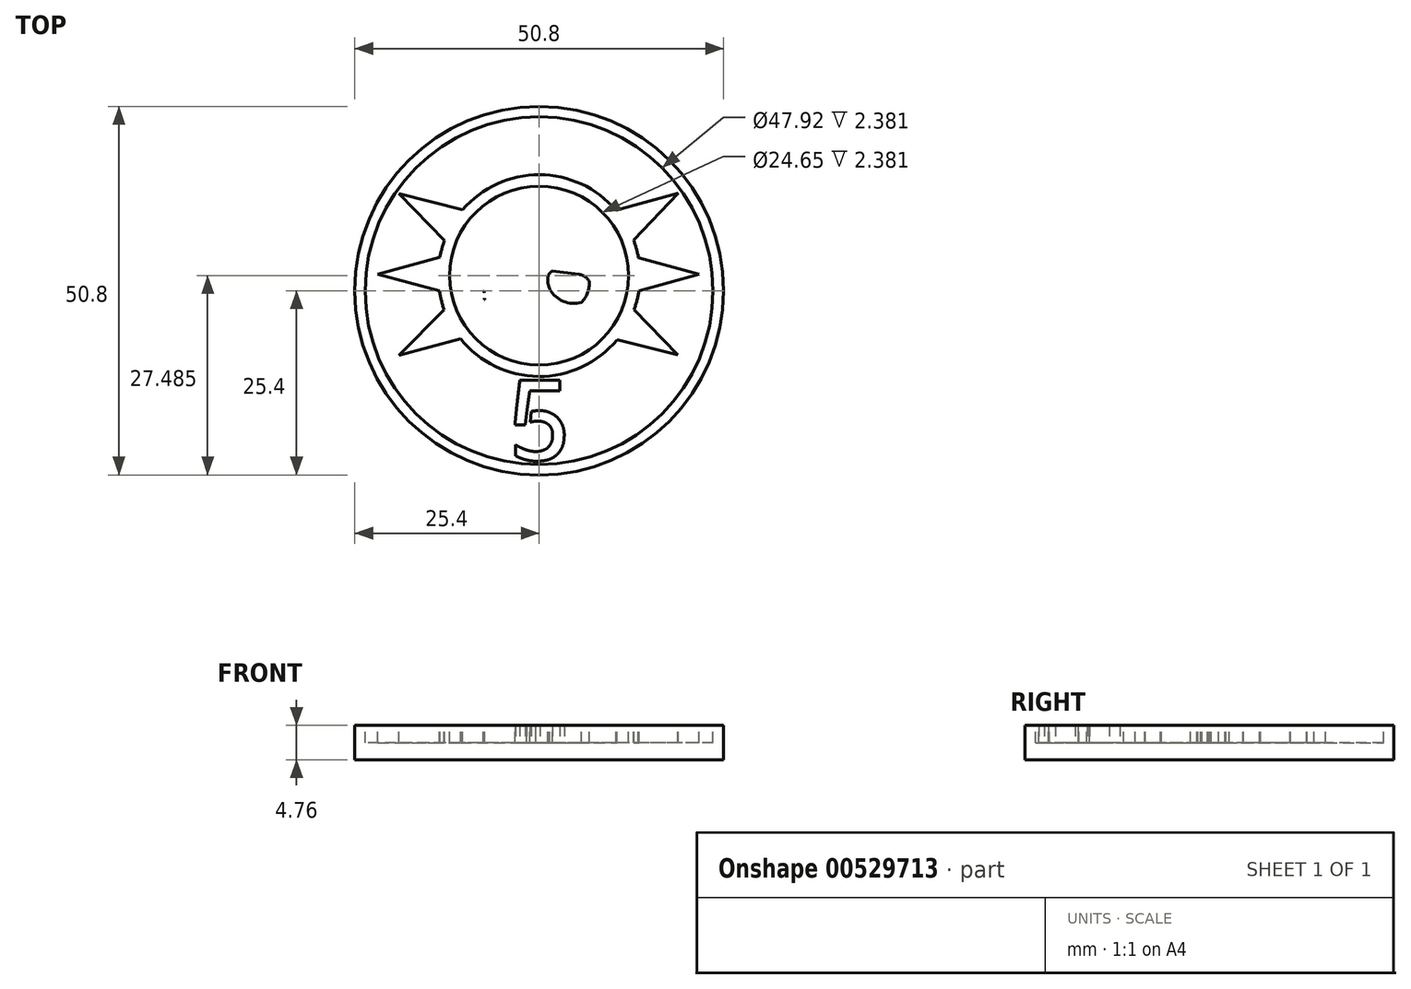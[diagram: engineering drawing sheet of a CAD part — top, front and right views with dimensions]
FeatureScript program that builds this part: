
annotation { "Feature Type Name" : "Feature", "Feature Type Description" : "" }
export const myFeature = defineFeature(function(context is Context, id is Id, definition is map)
    precondition{}
    {
        {
            var Q0;
            Q0=qCreatedBy(makeId("Top.planeOp"),FACE);
            var sketch = newSketch(context, id + "F0", { "sketchPlane" : qUnion([Q0])});
            skCircle(sketch, "E0", {"center": v(0, 0) * mm, "radius": 25.4 * mm});
            skSolve(sketch);
        }
        {
            var Q0;
            Q0=makeQuery(id+"F0.imprint","IMPRINT",FACE,{"disambiguationData":[TD([[makeQuery(id+"F0.imprint","IMPRINT",EDGE,{"derivedFrom":sQuery(id+"F0.wireOp",EDGE,"E0")}),1.0]])]});
            extrude(context, id + "F1", {"entities" : qUnion([Q0]), "depth" : 4.76 * mm, "offsetDistance" : 25.4 * mm});
        }
        {
            var Q0;
            Q0=makeQuery(id+"F1.opExtrude","CAP_FACE",FACE,{"disambiguationData":[OSD([sQuery(id+"F0.wireOp",EDGE,"E0")])],"isStart":false});
            var sketch = newSketch(context, id + "F2", { "sketchPlane" : qUnion([Q0])});
            skLineSegment(sketch, "E1", {"start": v(0, 0) * mm, "end": v(0, 25.4) * mm});
            skArc(sketch, "E2", {"start": v(-0.33, 11.95) * mm, "mid": v(-7.7, 8.08) * mm, "end": v(-7.55, -0.24) * mm});
            skLineSegment(sketch, "E3", {"start": v(-7.48, -1.06) * mm, "end": v(-7.73, -1.69) * mm});
            skArc(sketch, "E4", {"start": v(-7.55, -1.24) * mm, "mid": v(-7.44, -0.63) * mm, "end": v(-7.66, -0.06) * mm});
            skLineSegment(sketch, "E5", {"start": v(-6.9, -4.41) * mm, "end": v(-4.69, -4.62) * mm});
            skLineSegment(sketch, "E6", {"start": v(-4.56, -4.7) * mm, "end": v(-4.14, -5.5) * mm});
            skLineSegment(sketch, "E7", {"start": v(-4.12, -5.57) * mm, "end": v(-4.12, -6.26) * mm});
            skLineSegment(sketch, "E8", {"start": v(-3.62, -5.79) * mm, "end": v(-3.62, -6.3) * mm});
            skLineSegment(sketch, "E9", {"start": v(-3.22, -5.83) * mm, "end": v(-3.22, -6.7) * mm});
            skLineSegment(sketch, "E10", {"start": v(-2.5, -6.15) * mm, "end": v(-2.5, -6.76) * mm});
            skLineSegment(sketch, "E11", {"start": v(-1.96, -6.2) * mm, "end": v(-1.96, -7.04) * mm});
            skLineSegment(sketch, "E12", {"start": v(-1.28, -6.38) * mm, "end": v(-1.28, -7.15) * mm});
            skLineSegment(sketch, "E13", {"start": v(-0.76, -6.38) * mm, "end": v(-0.76, -7.25) * mm});
            skLineSegment(sketch, "E14", {"start": v(0, -6.43) * mm, "end": v(0, -7.2) * mm});
            skLineSegment(sketch, "E15", {"start": v(0.42, -6.43) * mm, "end": v(0.42, -7.2) * mm});
            skLineSegment(sketch, "E16", {"start": v(1.1, -6.35) * mm, "end": v(1.1, -7.2) * mm});
            skLineSegment(sketch, "E17", {"start": v(1.66, -6.3) * mm, "end": v(1.66, -6.98) * mm});
            skLineSegment(sketch, "E18", {"start": v(2.3, -6.14) * mm, "end": v(2.3, -6.97) * mm});
            skLineSegment(sketch, "E19", {"start": v(2.65, -6.1) * mm, "end": v(2.71, -6.42) * mm});
            skLineSegment(sketch, "E20", {"start": v(3.3, -5.72) * mm, "end": v(3.84, -4.99) * mm});
            skLineSegment(sketch, "E21", {"start": v(6.1, -4.92) * mm, "end": v(3.97, -4.92) * mm});
            skLineSegment(sketch, "E22", {"start": v(-5.43, 2.26) * mm, "end": v(-1.82, 2.72) * mm});
            skPoint(sketch, "E23", {"position": v(-6.9, 1.26) * mm});
            skPoint(sketch, "E24", {"position": v(-5.8, -1.59) * mm});
            skPoint(sketch, "E25", {"position": v(-1.48, 0.2) * mm});
            skPoint(sketch, "E26", {"position": v(-1.26, 2.12) * mm});
            skArc(sketch, "E27", {"start": v(-7.73, -1.69) * mm, "mid": v(-7.8, -3.16) * mm, "end": v(-6.97, -4.38) * mm});
            skPoint(sketch, "E28.visualSharp", {"position": v(-6.94, -4.4) * mm});
            skArc(sketch, "E28.filletArc", {"start": v(-6.97, -4.38) * mm, "mid": v(-6.93, -4.4) * mm, "end": v(-6.9, -4.41) * mm});
            skPoint(sketch, "E29.visualSharp", {"position": v(-4.6, -4.63) * mm});
            skArc(sketch, "E29.filletArc", {"start": v(-4.56, -4.7) * mm, "mid": v(-4.62, -4.65) * mm, "end": v(-4.69, -4.62) * mm});
            skArc(sketch, "E30", {"start": v(-5.43, 2.26) * mm, "mid": v(-6.29, 1.94) * mm, "end": v(-6.9, 1.26) * mm});
            skArc(sketch, "E31", {"start": v(-6.9, 1.26) * mm, "mid": v(-6.67, -0.28) * mm, "end": v(-5.8, -1.59) * mm});
            skArc(sketch, "E32", {"start": v(-1.48, 0.2) * mm, "mid": v(-1.2, 1.15) * mm, "end": v(-1.26, 2.12) * mm});
            skArc(sketch, "E33", {"start": v(-1.26, 2.12) * mm, "mid": v(-1.5, 2.46) * mm, "end": v(-1.82, 2.72) * mm});
            skArc(sketch, "E34", {"start": v(-5.8, -1.59) * mm, "mid": v(-3.33, -1.45) * mm, "end": v(-1.48, 0.2) * mm});
            skArc(sketch, "E35.MirrorCS", {"start": v(0.33, 11.95) * mm, "mid": v(7.7, 8.08) * mm, "end": v(7.55, -0.24) * mm});
            skArc(sketch, "E36.MirrorCS", {"start": v(5.43, 2.26) * mm, "mid": v(6.29, 1.94) * mm, "end": v(6.9, 1.26) * mm});
            skLineSegment(sketch, "E37.MirrorCS", {"start": v(5.43, 2.26) * mm, "end": v(1.82, 2.72) * mm});
            skArc(sketch, "E38.MirrorCS", {"start": v(1.26, 2.12) * mm, "mid": v(1.5, 2.46) * mm, "end": v(1.82, 2.72) * mm});
            skArc(sketch, "E39.MirrorCS", {"start": v(1.48, 0.2) * mm, "mid": v(1.2, 1.15) * mm, "end": v(1.26, 2.12) * mm});
            skArc(sketch, "E40.MirrorCS", {"start": v(5.8, -1.59) * mm, "mid": v(3.33, -1.45) * mm, "end": v(1.48, 0.2) * mm});
            skArc(sketch, "E41.MirrorCS", {"start": v(6.9, 1.26) * mm, "mid": v(6.67, -0.28) * mm, "end": v(5.8, -1.59) * mm});
            skPoint(sketch, "E42", {"position": v(7.37, -2.43) * mm});
            skArc(sketch, "E43", {"start": v(6.15, -4.91) * mm, "mid": v(7.22, -3.9) * mm, "end": v(7.37, -2.43) * mm});
            skArc(sketch, "E44", {"start": v(7.55, -0.24) * mm, "mid": v(7.04, -1.3) * mm, "end": v(7.37, -2.43) * mm});
            skArc(sketch, "E45", {"start": v(-0.29, -0.3) * mm, "mid": v(-0.58, -0.16) * mm, "end": v(-0.87, -0.3) * mm});
            skArc(sketch, "E46", {"start": v(-0.87, -0.3) * mm, "mid": v(-1.54, -1.45) * mm, "end": v(-1.95, -2.72) * mm});
            skArc(sketch, "E47", {"start": v(-1.95, -2.72) * mm, "mid": v(-1.93, -3.53) * mm, "end": v(-1.73, -4.31) * mm});
            skArc(sketch, "E48", {"start": v(-1.73, -4.31) * mm, "mid": v(-0.75, -4.14) * mm, "end": v(-0.11, -3.38) * mm});
            skLineSegment(sketch, "E49", {"start": v(-0.29, -0.3) * mm, "end": v(-0.08, -0.82) * mm});
            skLineSegment(sketch, "E50.MirrorCS", {"start": v(0.29, -0.3) * mm, "end": v(0.08, -0.82) * mm});
            skArc(sketch, "E51.MirrorCS", {"start": v(0.29, -0.3) * mm, "mid": v(0.58, -0.16) * mm, "end": v(0.87, -0.3) * mm});
            skArc(sketch, "E52.MirrorCS", {"start": v(0.87, -0.3) * mm, "mid": v(1.54, -1.45) * mm, "end": v(1.95, -2.72) * mm});
            skArc(sketch, "E53.MirrorCS", {"start": v(1.95, -2.72) * mm, "mid": v(1.93, -3.53) * mm, "end": v(1.73, -4.31) * mm});
            skArc(sketch, "E54.MirrorCS", {"start": v(1.73, -4.31) * mm, "mid": v(0.75, -4.14) * mm, "end": v(0.11, -3.38) * mm});
            skPoint(sketch, "E55", {"position": v(0, -1.04) * mm});
            skPoint(sketch, "E56", {"position": v(0, -3.17) * mm});
            skLineSegment(sketch, "E57", {"start": v(-0.11, -3.38) * mm, "end": v(0, -3.17) * mm});
            skLineSegment(sketch, "E58", {"start": v(0.11, -3.38) * mm, "end": v(0, -3.17) * mm});
            skLineSegment(sketch, "E59", {"start": v(-0.08, -0.82) * mm, "end": v(0, -1.04) * mm});
            skLineSegment(sketch, "E60", {"start": v(0.08, -0.82) * mm, "end": v(0, -1.04) * mm});
            skArc(sketch, "E61", {"start": v(-13.03, 6.93) * mm, "mid": v(-13.4, 5.8) * mm, "end": v(-13.66, 4.65) * mm});
            skLineSegment(sketch, "E62", {"start": v(-13.03, 6.93) * mm, "end": v(-19.34, 13.38) * mm});
            skLineSegment(sketch, "E63", {"start": v(-19.34, 13.38) * mm, "end": v(-10.54, 11.15) * mm});
            skLineSegment(sketch, "E64", {"start": v(-22.2, 2.3) * mm, "end": v(-13.66, 4.65) * mm});
            skLineSegment(sketch, "E65", {"start": v(-22.2, 2.3) * mm, "end": v(-13.74, 0) * mm});
            skLineSegment(sketch, "E66", {"start": v(-19.33, -8.88) * mm, "end": v(-13.09, -2.6) * mm});
            skLineSegment(sketch, "E67", {"start": v(-19.33, -8.88) * mm, "end": v(-10.83, -6.62) * mm});
            skLineSegment(sketch, "E68", {"start": v(19.09, -8.84) * mm, "end": v(10.7, -6.78) * mm});
            skLineSegment(sketch, "E69", {"start": v(19.09, -8.84) * mm, "end": v(13.08, -2.62) * mm});
            skLineSegment(sketch, "E70", {"start": v(22.04, 2.25) * mm, "end": v(13.74, 0) * mm});
            skLineSegment(sketch, "E71", {"start": v(22.04, 2.25) * mm, "end": v(13.67, 4.58) * mm});
            skLineSegment(sketch, "E72", {"start": v(19.17, 13.42) * mm, "end": v(13, 7) * mm});
            skLineSegment(sketch, "E73", {"start": v(19.17, 13.42) * mm, "end": v(10.58, 11.1) * mm});
            skArc(sketch, "E74.trimOffspring", {"start": v(-13.74, 0) * mm, "mid": v(-13.48, -1.31) * mm, "end": v(-13.09, -2.6) * mm});
            skArc(sketch, "E75.trimOffspring", {"start": v(-10.83, -6.62) * mm, "mid": v(-0.1, -11.82) * mm, "end": v(10.7, -6.78) * mm});
            skArc(sketch, "E76.trimOffspring", {"start": v(10.58, 11.1) * mm, "mid": v(0.03, 15.99) * mm, "end": v(-10.54, 11.15) * mm});
            skArc(sketch, "E77.trimOffspring", {"start": v(13.08, -2.62) * mm, "mid": v(13.48, -1.32) * mm, "end": v(13.74, 0) * mm});
            skArc(sketch, "E78.trimOffspring", {"start": v(13.67, 4.58) * mm, "mid": v(13.4, 5.8) * mm, "end": v(13, 7) * mm});
            skArc(sketch, "E79", {"start": v(-4.03, -6.4) * mm, "mid": v(-3.9, -6.44) * mm, "end": v(-3.77, -6.45) * mm});
            skArc(sketch, "E80", {"start": v(-3.2, -6.78) * mm, "mid": v(-2.9, -6.98) * mm, "end": v(-2.55, -6.87) * mm});
            skArc(sketch, "E81", {"start": v(-1.95, -7.1) * mm, "mid": v(-1.65, -7.34) * mm, "end": v(-1.29, -7.19) * mm});
            skArc(sketch, "E82", {"start": v(-0.64, -7.4) * mm, "mid": v(-0.36, -7.42) * mm, "end": v(-0.08, -7.34) * mm});
            skArc(sketch, "E83", {"start": v(0.45, -7.29) * mm, "mid": v(0.75, -7.45) * mm, "end": v(1.07, -7.3) * mm});
            skArc(sketch, "E84", {"start": v(1.7, -7.1) * mm, "mid": v(1.99, -7.21) * mm, "end": v(2.26, -7.07) * mm});
            skLineSegment(sketch, "E85", {"start": v(2.94, -6) * mm, "end": v(3.03, -6.42) * mm});
            skLineSegment(sketch, "E86", {"start": v(3.22, -5.78) * mm, "end": v(3.05, -5.82) * mm});
            skLineSegment(sketch, "E87", {"start": v(2.43, -5.98) * mm, "end": v(2.38, -6) * mm});
            skLineSegment(sketch, "E88", {"start": v(1.47, -6.15) * mm, "end": v(1.24, -6.2) * mm});
            skLineSegment(sketch, "E89", {"start": v(0.25, -6.27) * mm, "end": v(0.15, -6.28) * mm});
            skLineSegment(sketch, "E90", {"start": v(-0.9, -6.23) * mm, "end": v(-1.11, -6.22) * mm});
            skLineSegment(sketch, "E91", {"start": v(-2.1, -6.04) * mm, "end": v(-2.31, -6) * mm});
            skLineSegment(sketch, "E92", {"start": v(-3.31, -5.69) * mm, "end": v(-3.4, -5.65) * mm});
            skPoint(sketch, "E93.visualSharp", {"position": v(-0.76, -7.35) * mm});
            skArc(sketch, "E93.filletArc", {"start": v(-0.76, -7.25) * mm, "mid": v(-0.72, -7.34) * mm, "end": v(-0.64, -7.4) * mm});
            skPoint(sketch, "E94.visualSharp", {"position": v(0, -7.29) * mm});
            skArc(sketch, "E94.filletArc", {"start": v(-0.08, -7.34) * mm, "mid": v(-0.02, -7.28) * mm, "end": v(0, -7.2) * mm});
            skPoint(sketch, "E95.visualSharp", {"position": v(0.42, -7.24) * mm});
            skArc(sketch, "E95.filletArc", {"start": v(0.42, -7.2) * mm, "mid": v(0.43, -7.24) * mm, "end": v(0.45, -7.29) * mm});
            skPoint(sketch, "E96.visualSharp", {"position": v(1.1, -7.25) * mm});
            skArc(sketch, "E96.filletArc", {"start": v(1.07, -7.3) * mm, "mid": v(1.1, -7.26) * mm, "end": v(1.1, -7.2) * mm});
            skPoint(sketch, "E97.visualSharp", {"position": v(0.42, -6.26) * mm});
            skArc(sketch, "E97.filletArc", {"start": v(0.42, -6.43) * mm, "mid": v(0.37, -6.32) * mm, "end": v(0.25, -6.27) * mm});
            skPoint(sketch, "E98.visualSharp", {"position": v(0, -6.28) * mm});
            skArc(sketch, "E98.filletArc", {"start": v(0.15, -6.28) * mm, "mid": v(0.04, -6.32) * mm, "end": v(0, -6.43) * mm});
            skPoint(sketch, "E99.visualSharp", {"position": v(-1.28, -6.21) * mm});
            skArc(sketch, "E99.filletArc", {"start": v(-1.11, -6.22) * mm, "mid": v(-1.23, -6.26) * mm, "end": v(-1.28, -6.38) * mm});
            skPoint(sketch, "E100.visualSharp", {"position": v(-0.76, -6.23) * mm});
            skArc(sketch, "E100.filletArc", {"start": v(-0.76, -6.38) * mm, "mid": v(-0.8, -6.27) * mm, "end": v(-0.9, -6.23) * mm});
            skPoint(sketch, "E101.visualSharp", {"position": v(-1.96, -6.06) * mm});
            skArc(sketch, "E101.filletArc", {"start": v(-1.96, -6.2) * mm, "mid": v(-2, -6.1) * mm, "end": v(-2.1, -6.04) * mm});
            skPoint(sketch, "E102.visualSharp", {"position": v(-2.5, -5.96) * mm});
            skArc(sketch, "E102.filletArc", {"start": v(-2.31, -6) * mm, "mid": v(-2.44, -6.03) * mm, "end": v(-2.5, -6.15) * mm});
            skPoint(sketch, "E103.visualSharp", {"position": v(-3.22, -5.73) * mm});
            skArc(sketch, "E103.filletArc", {"start": v(-3.22, -5.83) * mm, "mid": v(-3.25, -5.74) * mm, "end": v(-3.31, -5.69) * mm});
            skPoint(sketch, "E104.visualSharp", {"position": v(-3.62, -5.54) * mm});
            skArc(sketch, "E104.filletArc", {"start": v(-3.4, -5.65) * mm, "mid": v(-3.55, -5.66) * mm, "end": v(-3.62, -5.79) * mm});
            skPoint(sketch, "E105.visualSharp", {"position": v(-4.12, -5.53) * mm});
            skArc(sketch, "E105.filletArc", {"start": v(-4.12, -5.57) * mm, "mid": v(-4.12, -5.53) * mm, "end": v(-4.14, -5.5) * mm});
            skPoint(sketch, "E106.visualSharp", {"position": v(-4.12, -6.35) * mm});
            skArc(sketch, "E106.filletArc", {"start": v(-4.12, -6.26) * mm, "mid": v(-4.1, -6.34) * mm, "end": v(-4.03, -6.4) * mm});
            skPoint(sketch, "E107.visualSharp", {"position": v(-3.62, -6.42) * mm});
            skArc(sketch, "E107.filletArc", {"start": v(-3.77, -6.45) * mm, "mid": v(-3.67, -6.4) * mm, "end": v(-3.62, -6.3) * mm});
            skPoint(sketch, "E108.visualSharp", {"position": v(-3.22, -6.73) * mm});
            skArc(sketch, "E108.filletArc", {"start": v(-3.22, -6.7) * mm, "mid": v(-3.22, -6.74) * mm, "end": v(-3.2, -6.78) * mm});
            skPoint(sketch, "E109.visualSharp", {"position": v(-2.5, -6.82) * mm});
            skArc(sketch, "E109.filletArc", {"start": v(-2.55, -6.87) * mm, "mid": v(-2.51, -6.82) * mm, "end": v(-2.5, -6.76) * mm});
            skPoint(sketch, "E110.visualSharp", {"position": v(-1.96, -7.07) * mm});
            skArc(sketch, "E110.filletArc", {"start": v(-1.96, -7.04) * mm, "mid": v(-1.96, -7.07) * mm, "end": v(-1.95, -7.1) * mm});
            skPoint(sketch, "E111.visualSharp", {"position": v(1.1, -6.21) * mm});
            skArc(sketch, "E111.filletArc", {"start": v(1.24, -6.2) * mm, "mid": v(1.14, -6.24) * mm, "end": v(1.1, -6.35) * mm});
            skPoint(sketch, "E112.visualSharp", {"position": v(1.66, -6.11) * mm});
            skArc(sketch, "E112.filletArc", {"start": v(1.66, -6.3) * mm, "mid": v(1.6, -6.18) * mm, "end": v(1.47, -6.15) * mm});
            skPoint(sketch, "E113.visualSharp", {"position": v(1.66, -7.04) * mm});
            skArc(sketch, "E113.filletArc", {"start": v(1.66, -6.98) * mm, "mid": v(1.67, -7.04) * mm, "end": v(1.7, -7.1) * mm});
            skPoint(sketch, "E114.visualSharp", {"position": v(2.3, -7.02) * mm});
            skArc(sketch, "E114.filletArc", {"start": v(2.26, -7.07) * mm, "mid": v(2.29, -7.02) * mm, "end": v(2.3, -6.97) * mm});
            skPoint(sketch, "E115.visualSharp", {"position": v(2.3, -6.05) * mm});
            skArc(sketch, "E115.filletArc", {"start": v(2.38, -6) * mm, "mid": v(2.32, -6.06) * mm, "end": v(2.3, -6.14) * mm});
            skPoint(sketch, "E116.visualSharp", {"position": v(2.62, -5.88) * mm});
            skArc(sketch, "E116.filletArc", {"start": v(2.65, -6.1) * mm, "mid": v(2.57, -5.98) * mm, "end": v(2.43, -5.98) * mm});
            skPoint(sketch, "E117.visualSharp", {"position": v(2.9, -5.85) * mm});
            skArc(sketch, "E117.filletArc", {"start": v(3.05, -5.82) * mm, "mid": v(2.96, -5.89) * mm, "end": v(2.94, -6) * mm});
            skPoint(sketch, "E118.visualSharp", {"position": v(3.27, -5.76) * mm});
            skArc(sketch, "E118.filletArc", {"start": v(3.22, -5.78) * mm, "mid": v(3.27, -5.75) * mm, "end": v(3.3, -5.72) * mm});
            skPoint(sketch, "E119.visualSharp", {"position": v(3.9, -4.92) * mm});
            skArc(sketch, "E119.filletArc", {"start": v(3.97, -4.92) * mm, "mid": v(3.9, -4.94) * mm, "end": v(3.84, -4.99) * mm});
            skPoint(sketch, "E120.visualSharp", {"position": v(6.12, -4.92) * mm});
            skArc(sketch, "E120.filletArc", {"start": v(6.1, -4.92) * mm, "mid": v(6.12, -4.92) * mm, "end": v(6.15, -4.91) * mm});
            skArc(sketch, "E121", {"start": v(2.93, -6.53) * mm, "mid": v(2.97, -6.51) * mm, "end": v(3, -6.48) * mm});
            skPoint(sketch, "E122.visualSharp", {"position": v(2.73, -6.53) * mm});
            skArc(sketch, "E122.filletArc", {"start": v(2.71, -6.42) * mm, "mid": v(2.8, -6.53) * mm, "end": v(2.93, -6.53) * mm});
            skPoint(sketch, "E123.visualSharp", {"position": v(3.03, -6.45) * mm});
            skArc(sketch, "E123.filletArc", {"start": v(3, -6.48) * mm, "mid": v(3.03, -6.45) * mm, "end": v(3.03, -6.42) * mm});
            skLineSegment(sketch, "E124", {"start": v(-0.33, 11.95) * mm, "end": v(0.33, 11.95) * mm});
            skPoint(sketch, "E125.orphan", {"position": v(0, 11.92) * mm});
            skCircle(sketch, "E126", {"center": v(0, 2.09) * mm, "radius": 12.32 * mm});
            skPoint(sketch, "E127.visualSharp", {"position": v(-1.28, -7.17) * mm});
            skArc(sketch, "E127.filletArc", {"start": v(-1.29, -7.19) * mm, "mid": v(-1.28, -7.17) * mm, "end": v(-1.28, -7.15) * mm});
            skCircle(sketch, "E128", {"center": v(0, 0) * mm, "radius": 23.96 * mm});
            skSolve(sketch);
        }
        {
            var Q0;
            Q0=qSketchRegion(id+"F2",true);
            var Q1;
            Q1=makeQuery(id+"F2.imprint","IMPRINT",FACE,{"disambiguationData":[TD([[makeQuery(id+"F2.imprint","IMPRINT",EDGE,{"derivedFrom":sQuery(id+"F2.wireOp",EDGE,"E22")}),-1.0]])]});
            var Q2;
            Q2=makeQuery(id+"F2.imprint","IMPRINT",FACE,{"disambiguationData":[TD([[makeQuery(id+"F2.imprint","IMPRINT",EDGE,{"derivedFrom":sQuery(id+"F2.wireOp",EDGE,"E36.MirrorCS")}),-1.0]])]});
            var Q3;
            Q3=makeQuery(id+"F2.imprint","IMPRINT",FACE,{"disambiguationData":[TD([[makeQuery(id+"F2.imprint","IMPRINT",EDGE,{"derivedFrom":sQuery(id+"F2.wireOp",EDGE,"E5")}),-1.0]])]});
            var Q4;
            Q4=makeQuery(id+"F2.imprint","IMPRINT",FACE,{"disambiguationData":[TD([[makeQuery(id+"F2.imprint","IMPRINT",EDGE,{"derivedFrom":sQuery(id+"F2.wireOp",EDGE,"E45")}),1.0]])]});
            extrude(context, id + "F3", {"entities" : qUnion([Q0, Q1, Q2, Q3, Q4]), "operationType" : NewBodyOperationType.REMOVE, "oppositeDirection" : true, "depth" : 2.38 * mm, "offsetDistance" : 25.4 * mm});
        }
        {
            var Q0;
            Q0=makeQuery(id+"F3.boolean.opBoolean","COPY",FACE,{"derivedFrom":makeQuery(id+"F3.opExtrude","CAP_FACE",FACE,{"disambiguationData":[OSD([sQuery(id+"F2.wireOp",EDGE,"E61"),sQuery(id+"F2.wireOp",EDGE,"E62"),sQuery(id+"F2.wireOp",EDGE,"E63"),sQuery(id+"F2.wireOp",EDGE,"E64"),sQuery(id+"F2.wireOp",EDGE,"E65"),sQuery(id+"F2.wireOp",EDGE,"E66"),sQuery(id+"F2.wireOp",EDGE,"E67"),sQuery(id+"F2.wireOp",EDGE,"E68"),sQuery(id+"F2.wireOp",EDGE,"E69"),sQuery(id+"F2.wireOp",EDGE,"E70"),sQuery(id+"F2.wireOp",EDGE,"E71"),sQuery(id+"F2.wireOp",EDGE,"E72"),sQuery(id+"F2.wireOp",EDGE,"E73"),sQuery(id+"F2.wireOp",EDGE,"E74.trimOffspring"),sQuery(id+"F2.wireOp",EDGE,"E75.trimOffspring"),sQuery(id+"F2.wireOp",EDGE,"E76.trimOffspring"),sQuery(id+"F2.wireOp",EDGE,"E77.trimOffspring"),sQuery(id+"F2.wireOp",EDGE,"E78.trimOffspring"),sQuery(id+"F2.wireOp",EDGE,"E128")])],"isStart":false})});
            var sketch = newSketch(context, id + "F4", { "sketchPlane" : qUnion([Q0])});
            skPoint(sketch, "E129", {"position": v(-4.5, -12.32) * mm});
            skPoint(sketch, "E130", {"position": v(4.5, -23.43) * mm});
            skText(sketch, "E131", { "text": "5", "fontName": "AllertaStencil-Regular.ttf"});
            const initialGuessF4  = {"E131": [-0.0045, -0.02343, 1, 0, 0.01111]};
            skSetInitialGuess(sketch, initialGuessF4);
            skSolve(sketch);
        }
        {
            var Q0;
            Q0=qSketchRegion(id+"F4",true);
            extrude(context, id + "F5", {"entities" : qUnion([Q0]), "operationType" : NewBodyOperationType.ADD, "depth" : 2.38 * mm, "offsetDistance" : 25.4 * mm});
        }
    });
